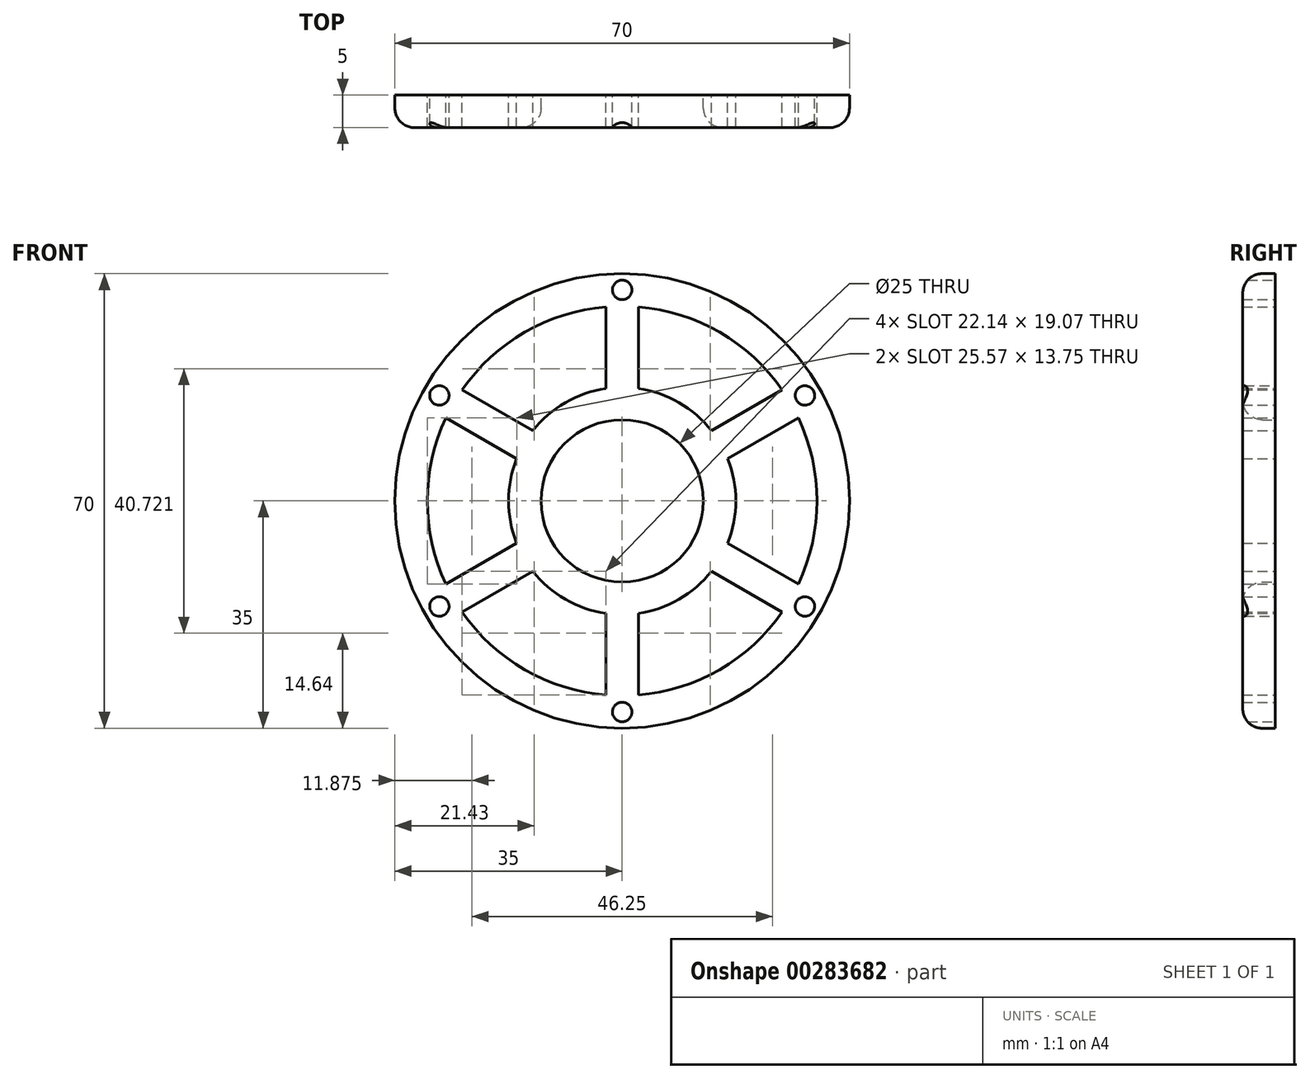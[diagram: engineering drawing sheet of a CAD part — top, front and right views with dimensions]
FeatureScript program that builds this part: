
annotation { "Feature Type Name" : "Feature", "Feature Type Description" : "" }
export const myFeature = defineFeature(function(context is Context, id is Id, definition is map)
    precondition{}
    {
        {
            var Q0;
            Q0=qCreatedBy(makeId("Front.planeOp"),FACE);
            var sketch = newSketch(context, id + "F0", { "sketchPlane" : qUnion([Q0])});
            skArc(sketch, "E0", {"start": v(-27.14, 12.78) * mm, "mid": v(-30, 0) * mm, "end": v(-27.14, -12.78) * mm});
            skCircle(sketch, "E1", {"center": v(0, 0) * mm, "radius": 35 * mm});
            skPoint(sketch, "E2", {"position": v(0, 32.5) * mm});
            skPoint(sketch, "E3.1.0", {"position": v(28.15, 16.25) * mm});
            skPoint(sketch, "E3.2.0", {"position": v(28.15, -16.25) * mm});
            skPoint(sketch, "E3.3.0", {"position": v(0, -32.5) * mm});
            skPoint(sketch, "E3.4.0", {"position": v(-28.15, -16.25) * mm});
            skPoint(sketch, "E3.5.0", {"position": v(-28.15, 16.25) * mm});
            skLineSegment(sketch, "E3.anchor1", {"start": v(0, 0) * mm, "end": v(0, 32.5) * mm, "construction": true});
            skLineSegment(sketch, "E3.anchor2", {"start": v(0, 0) * mm, "end": v(-28.15, 16.25) * mm, "construction": true});
            skCircle(sketch, "E4", {"center": v(0, 0) * mm, "radius": 12.5 * mm});
            skArc(sketch, "E5", {"start": v(-16.25, 6.5) * mm, "mid": v(-17.5, 0) * mm, "end": v(-16.25, -6.5) * mm});
            skLineSegment(sketch, "E6", {"start": v(-2.5, 17.32) * mm, "end": v(-2.5, 29.9) * mm});
            skLineSegment(sketch, "E7", {"start": v(2.5, 17.32) * mm, "end": v(2.5, 29.9) * mm});
            skLineSegment(sketch, "E8.1.0", {"start": v(-13.75, 10.83) * mm, "end": v(-24.64, 17.11) * mm});
            skLineSegment(sketch, "E8.1.1", {"start": v(-16.25, 6.5) * mm, "end": v(-27.14, 12.78) * mm});
            skLineSegment(sketch, "E8.2.0", {"start": v(-16.25, -6.5) * mm, "end": v(-27.14, -12.78) * mm});
            skLineSegment(sketch, "E8.2.1", {"start": v(-13.75, -10.83) * mm, "end": v(-24.64, -17.11) * mm});
            skLineSegment(sketch, "E8.3.0", {"start": v(-2.5, -17.32) * mm, "end": v(-2.5, -29.9) * mm});
            skLineSegment(sketch, "E8.3.1", {"start": v(2.5, -17.32) * mm, "end": v(2.5, -29.9) * mm});
            skLineSegment(sketch, "E8.4.0", {"start": v(13.75, -10.83) * mm, "end": v(24.64, -17.11) * mm});
            skLineSegment(sketch, "E8.4.1", {"start": v(16.25, -6.5) * mm, "end": v(27.14, -12.78) * mm});
            skLineSegment(sketch, "E8.5.0", {"start": v(16.25, 6.5) * mm, "end": v(27.14, 12.78) * mm});
            skLineSegment(sketch, "E8.5.1", {"start": v(13.75, 10.83) * mm, "end": v(24.64, 17.11) * mm});
            skArc(sketch, "E9.trimOffspring", {"start": v(-2.5, 17.32) * mm, "mid": v(-8.75, 15.16) * mm, "end": v(-13.75, 10.83) * mm});
            skArc(sketch, "E10.trimOffspring", {"start": v(-2.5, 29.9) * mm, "mid": v(-15, 25.98) * mm, "end": v(-24.64, 17.11) * mm});
            skArc(sketch, "E11.trimOffspring", {"start": v(24.64, 17.11) * mm, "mid": v(15, 25.98) * mm, "end": v(2.5, 29.9) * mm});
            skArc(sketch, "E12.trimOffspring", {"start": v(13.75, 10.83) * mm, "mid": v(8.75, 15.16) * mm, "end": v(2.5, 17.32) * mm});
            skArc(sketch, "E13.trimOffspring", {"start": v(16.25, -6.5) * mm, "mid": v(17.5, 0) * mm, "end": v(16.25, 6.5) * mm});
            skArc(sketch, "E14.trimOffspring", {"start": v(27.14, -12.78) * mm, "mid": v(30, 0) * mm, "end": v(27.14, 12.78) * mm});
            skArc(sketch, "E15.trimOffspring", {"start": v(2.5, -17.32) * mm, "mid": v(8.75, -15.16) * mm, "end": v(13.75, -10.83) * mm});
            skArc(sketch, "E16.trimOffspring", {"start": v(2.5, -29.9) * mm, "mid": v(15, -25.98) * mm, "end": v(24.64, -17.11) * mm});
            skArc(sketch, "E17.trimOffspring", {"start": v(-24.64, -17.11) * mm, "mid": v(-15, -25.98) * mm, "end": v(-2.5, -29.9) * mm});
            skArc(sketch, "E18.trimOffspring", {"start": v(-13.75, -10.83) * mm, "mid": v(-8.75, -15.16) * mm, "end": v(-2.5, -17.32) * mm});
            skSolve(sketch);
        }
        {
            var Q0;
            Q0=makeQuery(id+"F0.imprint","IMPRINT",FACE,{"disambiguationData":[TD([[makeQuery(id+"F0.imprint","IMPRINT",EDGE,{"derivedFrom":sQuery(id+"F0.wireOp",EDGE,"E0")}),-1.0]])]});
            extrude(context, id + "F1", {"entities" : qUnion([Q0]), "depth" : 5 * mm});
        }
        {
            var Q0;
            Q0=makeQuery(id+"F1.opExtrude","CAP_EDGE",EDGE,{"disambiguationData":[OSD([sQuery(id+"F0.wireOp",EDGE,"E1")])],"isStart":false});
            var Q1;
            Q1=makeQuery(id+"F1.opExtrude","CAP_EDGE",EDGE,{"disambiguationData":[OSD([sQuery(id+"F0.wireOp",EDGE,"E4")])],"isStart":false});
            fillet(context, id + "F2", {"entities" : qUnion([Q0, Q1]), "radius" : 3 * mm, "tangentPropagation" : true, "allowEdgeOverflow" : false});
        }
        {
            var Q0;
            Q0=sQuery(id+"F0.wireOp",VERTEX,"E3.4.0");
            var Q1;
            Q1=sQuery(id+"F0.wireOp",VERTEX,"E3.5.0");
            var Q2;
            Q2=sQuery(id+"F0.wireOp",VERTEX,"E2");
            var Q3;
            Q3=sQuery(id+"F0.wireOp",VERTEX,"E3.1.0");
            var Q4;
            Q4=sQuery(id+"F0.wireOp",VERTEX,"E3.2.0");
            var Q5;
            Q5=sQuery(id+"F0.wireOp",VERTEX,"E3.3.0");
            var Q6;
            Q6=makeQuery(id+"F1.opExtrude","SWEPT_BODY",BODY,{"disambiguationData":[OSD([sQuery(id+"F0.wireOp",EDGE,"E0"),sQuery(id+"F0.wireOp",EDGE,"E1"),sQuery(id+"F0.wireOp",EDGE,"E4"),sQuery(id+"F0.wireOp",EDGE,"E5"),sQuery(id+"F0.wireOp",EDGE,"E6"),sQuery(id+"F0.wireOp",EDGE,"E7"),sQuery(id+"F0.wireOp",EDGE,"E8.1.0"),sQuery(id+"F0.wireOp",EDGE,"E8.1.1"),sQuery(id+"F0.wireOp",EDGE,"E8.2.0"),sQuery(id+"F0.wireOp",EDGE,"E8.2.1"),sQuery(id+"F0.wireOp",EDGE,"E8.3.0"),sQuery(id+"F0.wireOp",EDGE,"E8.3.1"),sQuery(id+"F0.wireOp",EDGE,"E8.4.0"),sQuery(id+"F0.wireOp",EDGE,"E8.4.1"),sQuery(id+"F0.wireOp",EDGE,"E8.5.0"),sQuery(id+"F0.wireOp",EDGE,"E8.5.1"),sQuery(id+"F0.wireOp",EDGE,"E9.trimOffspring"),sQuery(id+"F0.wireOp",EDGE,"E10.trimOffspring"),sQuery(id+"F0.wireOp",EDGE,"E11.trimOffspring"),sQuery(id+"F0.wireOp",EDGE,"E12.trimOffspring"),sQuery(id+"F0.wireOp",EDGE,"E13.trimOffspring"),sQuery(id+"F0.wireOp",EDGE,"E14.trimOffspring"),sQuery(id+"F0.wireOp",EDGE,"E15.trimOffspring"),sQuery(id+"F0.wireOp",EDGE,"E16.trimOffspring"),sQuery(id+"F0.wireOp",EDGE,"E17.trimOffspring"),sQuery(id+"F0.wireOp",EDGE,"E18.trimOffspring")])]});
            hole(context, id + "F3", {"style" : HoleStyle.SIMPLE, "endStyle" : HoleEndStyle.THROUGH, "oppositeDirection" : true, "holeDiameter" : 3 * mm, "tappedDepth" : 12 * mm, "tapClearance" : 3, "startFromSketch" : true, "locations" : qUnion([Q0, Q1, Q2, Q3, Q4, Q5]), "scope" : qUnion([Q6])});
        }
    });
